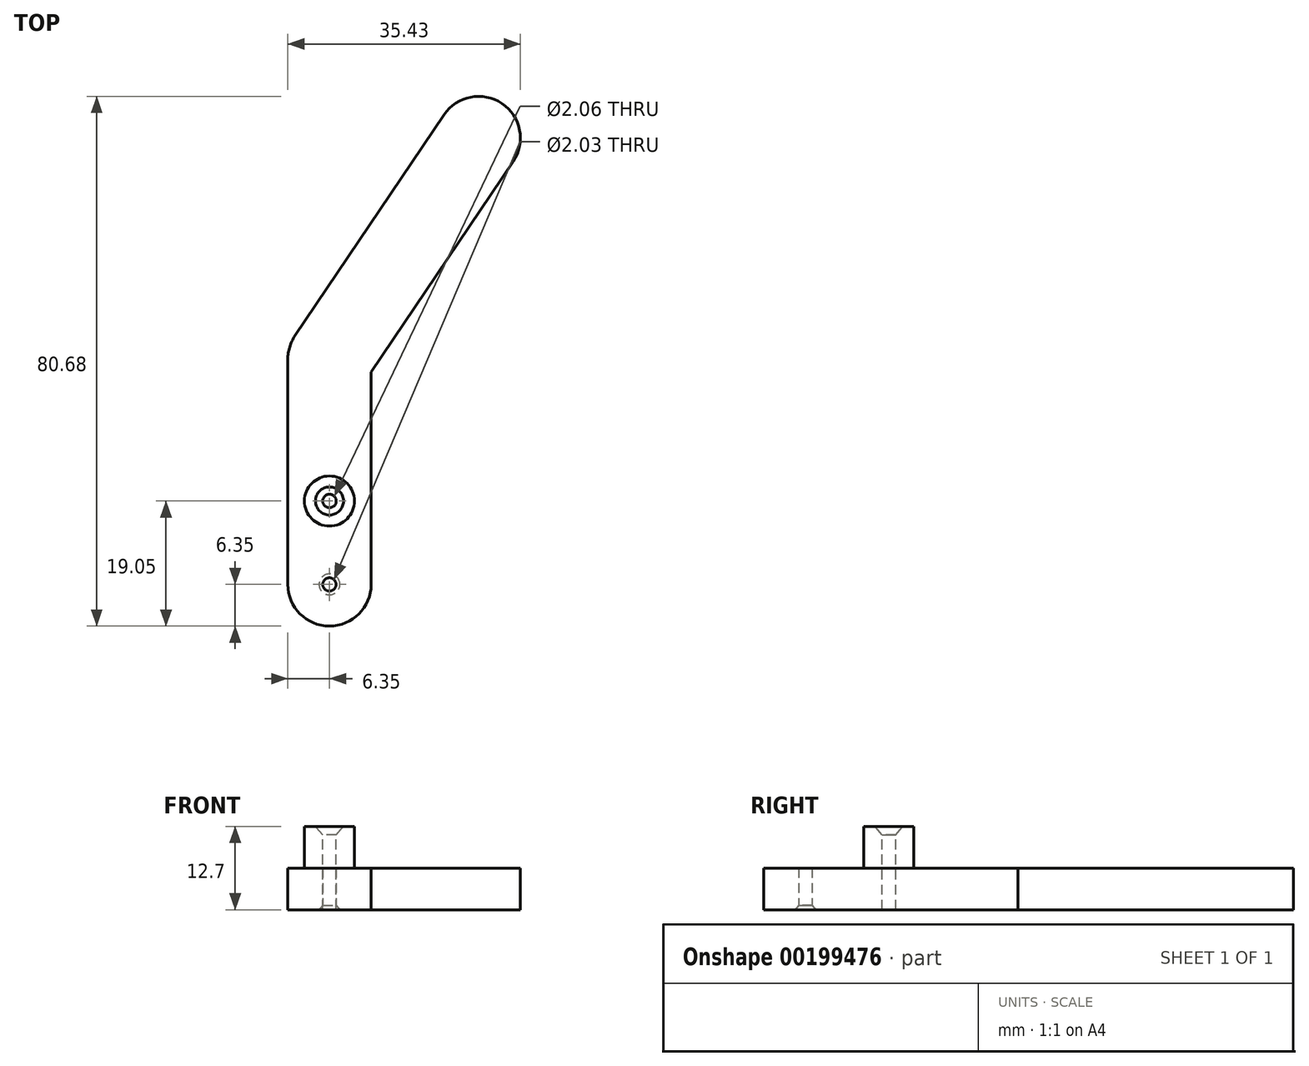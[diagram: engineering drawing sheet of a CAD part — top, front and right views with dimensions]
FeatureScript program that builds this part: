
annotation { "Feature Type Name" : "Feature", "Feature Type Description" : "" }
export const myFeature = defineFeature(function(context is Context, id is Id, definition is map)
    precondition{}
    {
        {
            var Q0;
            Q0=qCreatedBy(makeId("Top.planeOp"),FACE);
            var sketch = newSketch(context, id + "F0", { "sketchPlane" : qUnion([Q0])});
            skLineSegment(sketch, "E0", {"start": v(0, 0) * mm, "end": v(0, 12.7) * mm});
            skLineSegment(sketch, "E1", {"start": v(0, 12.7) * mm, "end": v(0, 34.3) * mm});
            skLineSegment(sketch, "E2", {"start": v(0, 34.3) * mm, "end": v(22.73, 67.98) * mm});
            skArc(sketch, "E3.0.startCap", {"start": v(5.26, 30.74) * mm, "mid": v(-3.55, 29.03) * mm, "end": v(-5.26, 37.84) * mm});
            skArc(sketch, "E3.0.endCap", {"start": v(17.46, 71.53) * mm, "mid": v(26.28, 73.25) * mm, "end": v(27.99, 64.43) * mm});
            skLineSegment(sketch, "E3.0.left", {"start": v(-5.26, 37.84) * mm, "end": v(17.46, 71.53) * mm});
            skLineSegment(sketch, "E3.0.right", {"start": v(5.26, 30.74) * mm, "end": v(27.99, 64.43) * mm});
            skArc(sketch, "E3.1.startCap", {"start": v(6.35, 0) * mm, "mid": v(0, -6.35) * mm, "end": v(-6.35, 0) * mm});
            skArc(sketch, "E3.1.endCap", {"start": v(-6.35, 12.7) * mm, "mid": v(0, 19.05) * mm, "end": v(6.35, 12.7) * mm});
            skLineSegment(sketch, "E3.1.left", {"start": v(-6.35, 0) * mm, "end": v(-6.35, 12.7) * mm});
            skLineSegment(sketch, "E3.1.right", {"start": v(6.35, 0) * mm, "end": v(6.35, 12.7) * mm});
            skArc(sketch, "E3.2.startCap", {"start": v(6.35, 12.7) * mm, "mid": v(0, 6.35) * mm, "end": v(-6.35, 12.7) * mm});
            skArc(sketch, "E3.2.endCap", {"start": v(-6.35, 34.3) * mm, "mid": v(0, 40.64) * mm, "end": v(6.35, 34.3) * mm});
            skLineSegment(sketch, "E3.2.left", {"start": v(-6.35, 12.7) * mm, "end": v(-6.35, 34.3) * mm});
            skLineSegment(sketch, "E3.2.right", {"start": v(6.35, 12.7) * mm, "end": v(6.35, 34.3) * mm});
            skSolve(sketch);
        }
        {
            var Q0;
            Q0 = qSketchRegion(id + "F0", true);
            extrude(context, id + "F1", {"entities" : qUnion([Q0]), "depth" : 6.35 * mm});
        }
        {
            var Q0;
            Q0=makeQuery(id+"F1.opExtrude","CAP_FACE",FACE,{"disambiguationData":[OSD([sQuery(id+"F0.wireOp",EDGE,"E3.0.endCap"),sQuery(id+"F0.wireOp",EDGE,"E3.0.left"),sQuery(id+"F0.wireOp",EDGE,"E3.0.right"),sQuery(id+"F0.wireOp",EDGE,"E3.1.startCap"),sQuery(id+"F0.wireOp",EDGE,"E3.1.left"),sQuery(id+"F0.wireOp",EDGE,"E3.1.right"),sQuery(id+"F0.wireOp",EDGE,"E3.2.endCap"),sQuery(id+"F0.wireOp",EDGE,"E3.2.left"),sQuery(id+"F0.wireOp",EDGE,"E3.2.right")])],"isStart":false});
            var sketch = newSketch(context, id + "F2", { "sketchPlane" : qUnion([Q0])});
            skCircle(sketch, "E4", {"center": v(0, 12.7) * mm, "radius": 3.81 * mm});
            skSolve(sketch);
        }
        {
            var Q0;
            Q0 = qSketchRegion(id + "F2", true);
            extrude(context, id + "F3", {"entities" : qUnion([Q0]), "operationType" : NewBodyOperationType.ADD, "depth" : 6.35 * mm});
        }
        {
            var Q0;
            Q0=makeQuery(id+"F3.opExtrude","CAP_FACE",FACE,{"disambiguationData":[OSD([sQuery(id+"F2.wireOp",EDGE,"E4")])],"isStart":false});
            var sketch = newSketch(context, id + "F4", { "sketchPlane" : qUnion([Q0])});
            skPoint(sketch, "E5", {"position": v(0, 12.7) * mm});
            skSolve(sketch);
        }
        {
            var Q0;
            Q0=sQuery(id+"F4.wireOp",VERTEX,"E5");
            var Q1;
            Q1=makeQuery(id+"F1.opExtrude","SWEPT_BODY",BODY,{"disambiguationData":[OSD([sQuery(id+"F0.wireOp",EDGE,"E3.0.endCap"),sQuery(id+"F0.wireOp",EDGE,"E3.0.left"),sQuery(id+"F0.wireOp",EDGE,"E3.0.right"),sQuery(id+"F0.wireOp",EDGE,"E3.1.startCap"),sQuery(id+"F0.wireOp",EDGE,"E3.1.left"),sQuery(id+"F0.wireOp",EDGE,"E3.1.right"),sQuery(id+"F0.wireOp",EDGE,"E3.2.endCap"),sQuery(id+"F0.wireOp",EDGE,"E3.2.left"),sQuery(id+"F0.wireOp",EDGE,"E3.2.right")])]});
            hole(context, id + "F5", {"style" : HoleStyle.C_SINK, "endStyle" : HoleEndStyle.THROUGH, "standardTappedOrClearance" : lookupTablePath({ "standard" : "ANSI", "fit" : "Normal (ASME)", "size" : "#1", "type" : "Clearance" }), "standardBlindInLast" : lookupTablePath({ "fit" : "Free", "standard" : "ANSI", "size" : "#1", "type" : "Clearance" }), "holeDiameter" : 2.06 * mm, "cSinkDiameter" : 4.27 * mm, "cSinkAngle" : 82 * degree, "locations" : qUnion([Q0]), "scope" : qUnion([Q1]), "isTappedThrough" : true});
        }
        {
            var Q0;
            Q0=sQuery(id+"F0.wireOp",VERTEX,"E3.1.startCap.center");
            var Q1;
            Q1=makeQuery(id+"F1.opExtrude","SWEPT_BODY",BODY,{"disambiguationData":[OSD([sQuery(id+"F0.wireOp",EDGE,"E3.0.endCap"),sQuery(id+"F0.wireOp",EDGE,"E3.0.left"),sQuery(id+"F0.wireOp",EDGE,"E3.0.right"),sQuery(id+"F0.wireOp",EDGE,"E3.1.startCap"),sQuery(id+"F0.wireOp",EDGE,"E3.1.left"),sQuery(id+"F0.wireOp",EDGE,"E3.1.right"),sQuery(id+"F0.wireOp",EDGE,"E3.2.endCap"),sQuery(id+"F0.wireOp",EDGE,"E3.2.left"),sQuery(id+"F0.wireOp",EDGE,"E3.2.right")])]});
            hole(context, id + "F6", {"style" : HoleStyle.C_SINK, "endStyle" : HoleEndStyle.THROUGH, "oppositeDirection" : true, "holeDiameter" : 2.03 * mm, "cSinkDiameter" : 3.17 * mm, "cSinkAngle" : 82 * degree, "locations" : qUnion([Q0]), "scope" : qUnion([Q1]), "isTappedThrough" : true});
        }
    });
